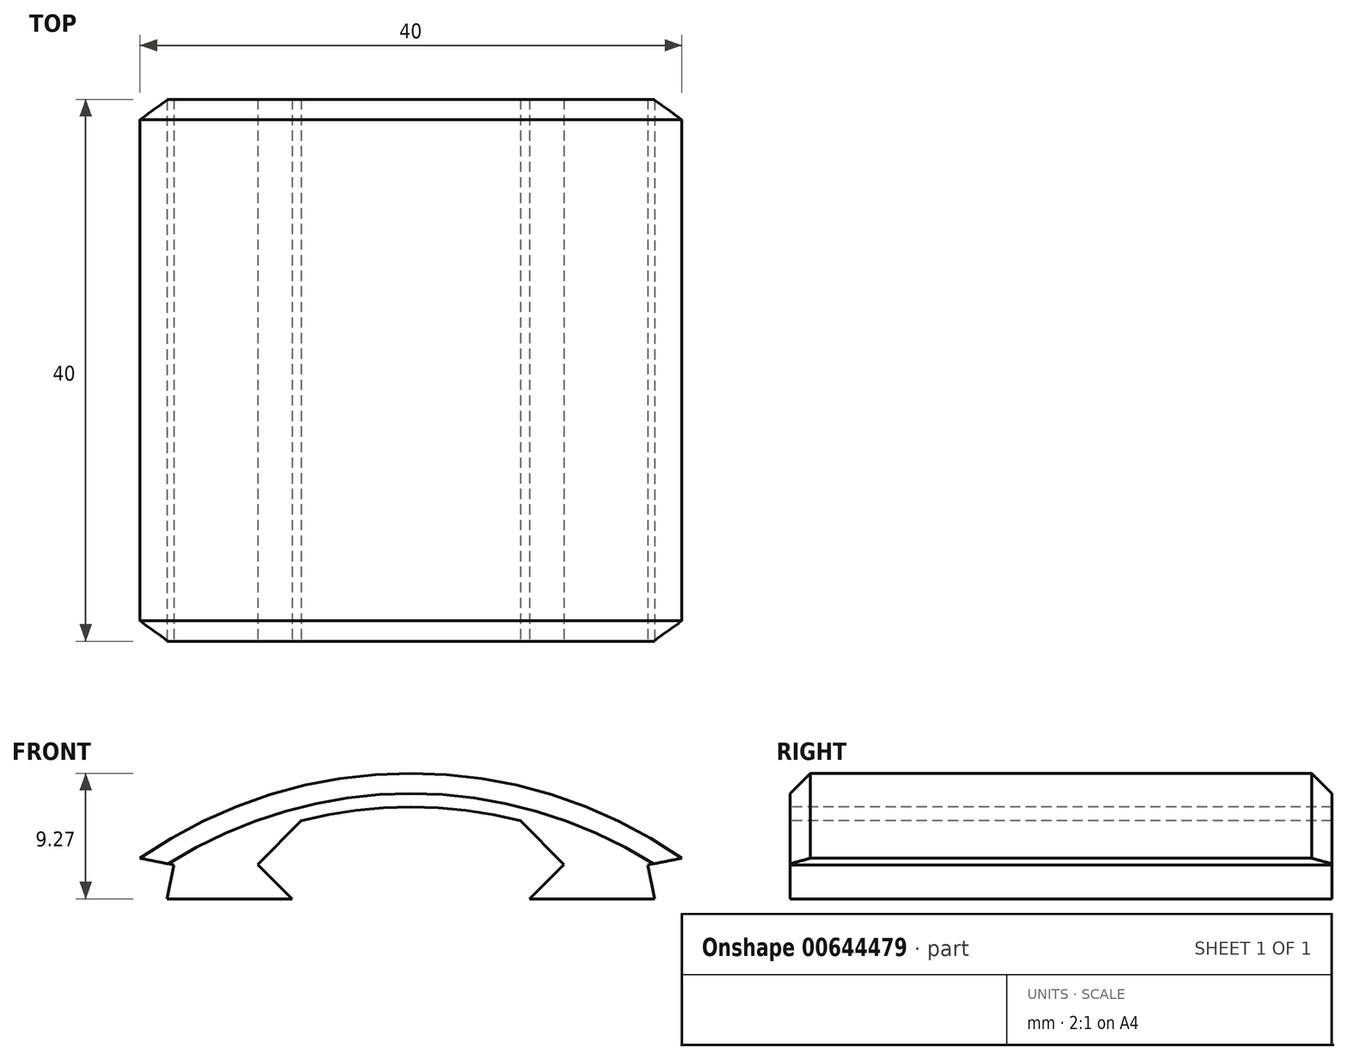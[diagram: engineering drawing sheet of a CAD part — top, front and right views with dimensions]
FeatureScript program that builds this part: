
annotation { "Feature Type Name" : "Feature", "Feature Type Description" : "" }
export const myFeature = defineFeature(function(context is Context, id is Id, definition is map)
    precondition{}
    {
        {
            var Q0;
            Q0=qCreatedBy(makeId("Front.planeOp"),FACE);
            var sketch = newSketch(context, id + "F0", { "sketchPlane" : qUnion([Q0])});
            skLineSegment(sketch, "E0", {"start": v(7.84, 9.32) * mm, "end": v(10.6, 6.56) * mm});
            skLineSegment(sketch, "E1", {"start": v(10.6, 6.55) * mm, "end": v(7.84, 3.8) * mm});
            skLineSegment(sketch, "E2", {"start": v(7.84, 3.8) * mm, "end": v(7.84, 0) * mm});
            skLineSegment(sketch, "E3.MirrorCS", {"start": v(-7.84, 9.32) * mm, "end": v(-10.6, 6.56) * mm});
            skLineSegment(sketch, "E4.MirrorCS", {"start": v(-7.84, 3.8) * mm, "end": v(-7.84, 0) * mm});
            skLineSegment(sketch, "E5.MirrorCS", {"start": v(-10.6, 6.56) * mm, "end": v(-7.84, 3.8) * mm});
            skLineSegment(sketch, "E6", {"start": v(8.77, 4.02) * mm, "end": v(18, 4.02) * mm});
            skLineSegment(sketch, "E7.MirrorCS", {"start": v(-8.77, 4.02) * mm, "end": v(-18, 4.02) * mm});
            skArc(sketch, "E8", {"start": v(20, 7.02) * mm, "mid": v(0, 13.3) * mm, "end": v(-20, 7.02) * mm});
            skLineSegment(sketch, "E9.0", {"start": v(-11.3, 6.56) * mm, "end": v(-8.77, 4.02) * mm});
            skLineSegment(sketch, "E9.1", {"start": v(-8.1, 9.77) * mm, "end": v(-11.3, 6.56) * mm});
            skLineSegment(sketch, "E9.2", {"start": v(11.3, 6.56) * mm, "end": v(8.77, 4.02) * mm});
            skLineSegment(sketch, "E9.3", {"start": v(8.1, 9.77) * mm, "end": v(11.3, 6.56) * mm});
            skLineSegment(sketch, "E10", {"start": v(-7.84, 0) * mm, "end": v(7.84, 0) * mm});
            skLineSegment(sketch, "E11", {"start": v(0, 27.78) * mm, "end": v(0, -34.47) * mm, "construction": true});
            skLineSegment(sketch, "E12", {"start": v(-27.45, -21.7) * mm, "end": v(32.31, -21.7) * mm, "construction": true});
            skLineSegment(sketch, "E13", {"start": v(-35, 13.3) * mm, "end": v(34.06, 13.3) * mm, "construction": true});
            skLineSegment(sketch, "E14", {"start": v(-20, 7.02) * mm, "end": v(-17.5, 6.52) * mm});
            skLineSegment(sketch, "E15", {"start": v(-17.5, 6.52) * mm, "end": v(-18, 4.02) * mm});
            skLineSegment(sketch, "E16", {"start": v(20, 7.02) * mm, "end": v(17.5, 6.52) * mm});
            skLineSegment(sketch, "E17", {"start": v(17.5, 6.52) * mm, "end": v(18, 4.02) * mm});
            skArc(sketch, "E18", {"start": v(-8.1, 9.77) * mm, "mid": v(0, 10.8) * mm, "end": v(8.1, 9.77) * mm});
            skLineSegment(sketch, "E19", {"start": v(-7.84, 9.32) * mm, "end": v(7.84, 9.32) * mm});
            skLineSegment(sketch, "E20", {"start": v(-18.6, 3.53) * mm, "end": v(-21.92, 0.21) * mm});
            skArc(sketch, "E21", {"start": v(-24.75, 3.04) * mm, "mid": v(-22.72, 4.91) * mm, "end": v(-20.56, 6.62) * mm});
            skLineSegment(sketch, "E22", {"start": v(0, -21.7) * mm, "end": v(-35, 13.3) * mm, "construction": true});
            skLineSegment(sketch, "E23.0", {"start": v(-20.56, 6.62) * mm, "end": v(-18.09, 6.12) * mm});
            skLineSegment(sketch, "E24.0", {"start": v(-18.09, 6.12) * mm, "end": v(-18.6, 3.53) * mm});
            skLineSegment(sketch, "E25.MirrorCS", {"start": v(-25.23, -3.1) * mm, "end": v(-21.92, 0.21) * mm});
            skLineSegment(sketch, "E26.MirrorCS", {"start": v(-27.83, -3.62) * mm, "end": v(-25.23, -3.1) * mm});
            skLineSegment(sketch, "E27.MirrorCS", {"start": v(-28.32, -1.15) * mm, "end": v(-27.83, -3.62) * mm});
            skArc(sketch, "E28.MirrorCS", {"start": v(-24.75, 3.04) * mm, "mid": v(-26.62, 1.02) * mm, "end": v(-28.32, -1.15) * mm});
            skPoint(sketch, "E29.orphan", {"position": v(-21.92, 0.21) * mm});
            skLineSegment(sketch, "E30", {"start": v(18, 4.02) * mm, "end": v(20, 7.02) * mm});
            skSolve(sketch);
        }
        {
            var Q0;
            Q0=makeQuery(id+"F0.imprint","IMPRINT",FACE,{"disambiguationData":[TD([[makeQuery(id+"F0.imprint","IMPRINT",EDGE,{"derivedFrom":sQuery(id+"F0.wireOp",EDGE,"E6")}),1.0]])]});
            var Q1;
            Q1=sQuery(id+"F0.wireOp",EDGE,"DqiW3eUc-Ietc-S6Wb-ShnJ-EKcXAPcgDz1b");
            var Q2;
            Q2=sQuery(id+"F0.wireOp",EDGE,"E8");
            var Q3;
            Q3=sQuery(id+"F0.wireOp",EDGE,"e0857c63-9742-4316-b3e5-f02756e2240e0.MirrorCS");
            var Q4;
            Q4=sQuery(id+"F0.wireOp",EDGE,"E7.MirrorCS");
            var Q5;
            Q5=sQuery(id+"F0.wireOp",EDGE,"E5.MirrorCS");
            var Q6;
            Q6=sQuery(id+"F0.wireOp",EDGE,"E3.MirrorCS");
            var Q7;
            Q7=sQuery(id+"F0.wireOp",EDGE,"efba849f-0844-4c9e-ada6-79df8e4986fb1.MirrorCS");
            var Q8;
            Q8=sQuery(id+"F0.wireOp",EDGE,"DCKnqX3q-fX6X-DB17-CLdz-X8ZRTvufnfF1");
            var Q9;
            Q9=sQuery(id+"F0.wireOp",EDGE,"E0");
            var Q10;
            Q10=sQuery(id+"F0.wireOp",EDGE,"E1");
            var Q11;
            Q11=sQuery(id+"F0.wireOp",EDGE,"E6");
            extrude(context, id + "F1", {"entities" : qUnion([Q0]), "surfaceEntities" : qUnion([Q1, Q2, Q3, Q4, Q5, Q6, Q7, Q8, Q9, Q10, Q11]), "oppositeDirection" : true, "depth" : 40 * mm, "offsetDistance" : 25 * mm});
        }
        {
            var Q0;
            Q0=makeQuery(id+"F1.opExtrude","CAP_EDGE",EDGE,{"disambiguationData":[OSD([sQuery(id+"F0.wireOp",EDGE,"E8")])],"isStart":true});
            var Q1;
            Q1=makeQuery(id+"F1.opExtrude","CAP_EDGE",EDGE,{"disambiguationData":[OSD([sQuery(id+"F0.wireOp",EDGE,"E8")])],"isStart":false});
            chamfer(context, id + "F2", {"entities" : qUnion([Q0, Q1]), "width" : 1.5 * mm, "tangentPropagation" : true});
        }
    });
